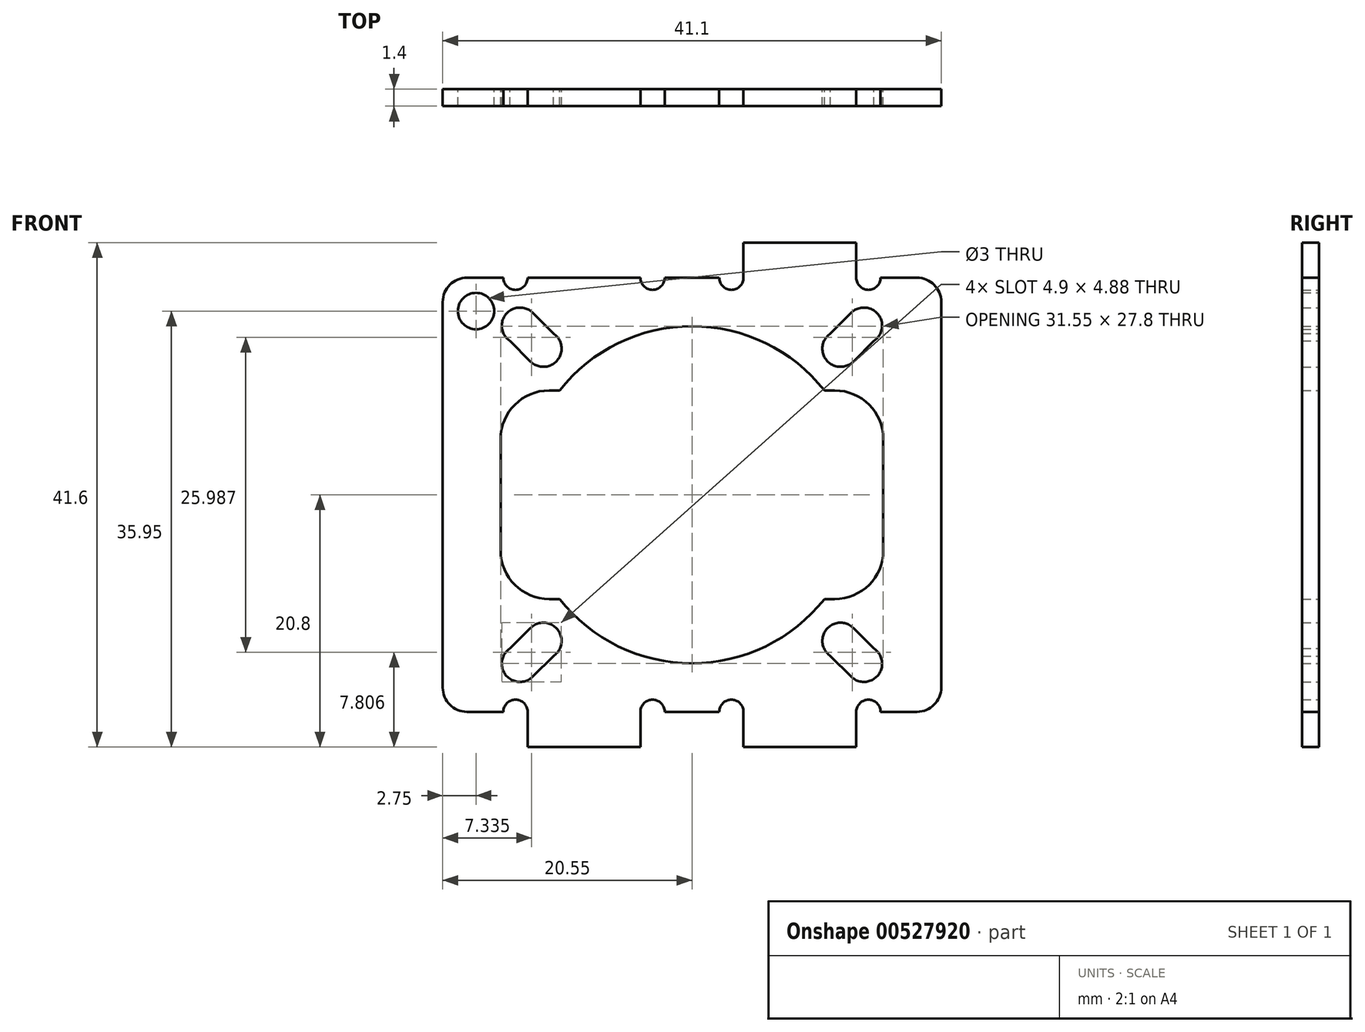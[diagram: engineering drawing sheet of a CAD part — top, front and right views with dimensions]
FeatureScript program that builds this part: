
annotation { "Feature Type Name" : "Feature", "Feature Type Description" : "" }
export const myFeature = defineFeature(function(context is Context, id is Id, definition is map)
    precondition{}
    {
        {
            var Q0;
            Q0=qCreatedBy(makeId("Front.planeOp"),FACE);
            var sketch = newSketch(context, id + "F0", { "sketchPlane" : qUnion([Q0])});
            skLineSegment(sketch, "E0.bottom", {"start": v(20.55, -17.9) * mm, "end": v(-20.55, -17.9) * mm});
            skLineSegment(sketch, "E0.top", {"start": v(20.55, 17.9) * mm, "end": v(-20.55, 17.9) * mm});
            skLineSegment(sketch, "E0.left", {"start": v(20.55, -17.9) * mm, "end": v(20.55, 17.9) * mm});
            skLineSegment(sketch, "E0.right", {"start": v(-20.55, -17.9) * mm, "end": v(-20.55, 17.9) * mm});
            skPoint(sketch, "E0.middle", {"position": v(0, 0) * mm});
            skCircle(sketch, "E1", {"center": v(0, 0) * mm, "radius": 13.9 * mm});
            skLineSegment(sketch, "E2.bottom", {"start": v(15.78, -8.6) * mm, "end": v(-15.78, -8.6) * mm});
            skLineSegment(sketch, "E2.top", {"start": v(15.78, 8.6) * mm, "end": v(-15.78, 8.6) * mm});
            skLineSegment(sketch, "E2.left", {"start": v(15.78, -8.6) * mm, "end": v(15.78, 8.6) * mm});
            skLineSegment(sketch, "E2.right", {"start": v(-15.78, -8.6) * mm, "end": v(-15.78, 8.6) * mm});
            skCircle(sketch, "E3", {"center": v(-14.18, 13.94) * mm, "radius": 1.5 * mm});
            skCircle(sketch, "E4", {"center": v(-12.25, 12.05) * mm, "radius": 1.5 * mm});
            skLineSegment(sketch, "E5", {"start": v(-15, 12.68) * mm, "end": v(-13.31, 10.99) * mm});
            skLineSegment(sketch, "E6", {"start": v(-11, 12.87) * mm, "end": v(-13.12, 15) * mm});
            skLineSegment(sketch, "E7.MirrorCS", {"start": v(-15, -12.68) * mm, "end": v(-13.31, -10.99) * mm});
            skCircle(sketch, "E8.MirrorC", {"center": v(-14.18, -13.94) * mm, "radius": 1.5 * mm});
            skCircle(sketch, "E9.MirrorC", {"center": v(-12.25, -12.05) * mm, "radius": 1.5 * mm});
            skLineSegment(sketch, "E10.MirrorCS", {"start": v(-11, -12.87) * mm, "end": v(-13.12, -15) * mm});
            skCircle(sketch, "E11.MirrorC", {"center": v(14.18, 13.94) * mm, "radius": 1.5 * mm});
            skCircle(sketch, "E12.MirrorC", {"center": v(12.25, 12.05) * mm, "radius": 1.5 * mm});
            skLineSegment(sketch, "E13.MirrorCS", {"start": v(15, 12.68) * mm, "end": v(13.31, 10.99) * mm});
            skLineSegment(sketch, "E14.MirrorCS", {"start": v(11, 12.87) * mm, "end": v(13.12, 15) * mm});
            skLineSegment(sketch, "E15.MirrorCS", {"start": v(15, -12.68) * mm, "end": v(13.31, -10.99) * mm});
            skCircle(sketch, "E16.MirrorC", {"center": v(14.18, -13.94) * mm, "radius": 1.5 * mm});
            skCircle(sketch, "E17.MirrorC", {"center": v(12.25, -12.05) * mm, "radius": 1.5 * mm});
            skLineSegment(sketch, "E18.MirrorCS", {"start": v(11, -12.87) * mm, "end": v(13.12, -15) * mm});
            skLineSegment(sketch, "E19", {"start": v(-28.19, 10.55) * mm, "end": v(24.82, 10.55) * mm, "construction": true});
            skLineSegment(sketch, "E20", {"start": v(-10.75, 26.36) * mm, "end": v(-10.75, 2.07) * mm, "construction": true});
            skLineSegment(sketch, "E21.bottom", {"start": v(-13.55, 17.9) * mm, "end": v(-4.25, 17.9) * mm});
            skLineSegment(sketch, "E21.top", {"start": v(-13.55, 20.8) * mm, "end": v(-4.25, 20.8) * mm});
            skLineSegment(sketch, "E21.left", {"start": v(-13.55, 17.9) * mm, "end": v(-13.55, 20.8) * mm});
            skLineSegment(sketch, "E21.right", {"start": v(-4.25, 17.9) * mm, "end": v(-4.25, 20.8) * mm});
            skLineSegment(sketch, "E22.MirrorCS", {"start": v(4.25, 17.9) * mm, "end": v(4.25, 20.8) * mm});
            skLineSegment(sketch, "E23.MirrorCS", {"start": v(13.55, 20.8) * mm, "end": v(4.25, 20.8) * mm});
            skLineSegment(sketch, "E24.MirrorCS", {"start": v(13.55, 17.9) * mm, "end": v(13.55, 20.8) * mm});
            skLineSegment(sketch, "E25.MirrorCS", {"start": v(-13.55, -17.9) * mm, "end": v(-13.55, -20.8) * mm});
            skLineSegment(sketch, "E26.MirrorCS", {"start": v(-13.55, -20.8) * mm, "end": v(-4.25, -20.8) * mm});
            skLineSegment(sketch, "E27.MirrorCS", {"start": v(-4.25, -17.9) * mm, "end": v(-4.25, -20.8) * mm});
            skLineSegment(sketch, "E28.MirrorCS", {"start": v(4.25, -17.9) * mm, "end": v(4.25, -20.8) * mm});
            skLineSegment(sketch, "E29.MirrorCS", {"start": v(13.55, -20.8) * mm, "end": v(4.25, -20.8) * mm});
            skLineSegment(sketch, "E30.MirrorCS", {"start": v(13.55, -17.9) * mm, "end": v(13.55, -20.8) * mm});
            skCircle(sketch, "E31", {"center": v(3.25, 17.9) * mm, "radius": 1 * mm});
            skCircle(sketch, "E32", {"center": v(-3.25, 17.9) * mm, "radius": 1 * mm});
            skCircle(sketch, "E33", {"center": v(-14.55, 17.9) * mm, "radius": 1 * mm});
            skCircle(sketch, "E34.MirrorC", {"center": v(-14.55, -17.9) * mm, "radius": 1 * mm});
            skCircle(sketch, "E35.MirrorC", {"center": v(-3.25, -17.9) * mm, "radius": 1 * mm});
            skCircle(sketch, "E36.MirrorC", {"center": v(3.25, -17.9) * mm, "radius": 1 * mm});
            skCircle(sketch, "E37", {"center": v(14.55, 17.9) * mm, "radius": 1 * mm});
            skCircle(sketch, "E38.MirrorC", {"center": v(14.55, -17.9) * mm, "radius": 1 * mm});
            skCircle(sketch, "E39", {"center": v(-17.8, 15.15) * mm, "radius": 1.5 * mm});
            skSolve(sketch);
        }
        {
            var Q0;
            Q0=makeQuery(id+"F0.imprint","IMPRINT",FACE,{"disambiguationData":[TD([[makeQuery(id+"F0.imprint","IMPRINT",EDGE,{"derivedFrom":sQuery(id+"F0.wireOp",EDGE,"E0.bottom")}),-1.0]])]});
            var Q1;
            Q1=makeQuery(id+"F0.imprint","IMPRINT",FACE,{"disambiguationData":[TD([[makeQuery(id+"F0.imprint","IMPRINT",EDGE,{"derivedFrom":sQuery(id+"F0.wireOp",EDGE,"E21.bottom")}),1.0]])]});
            var Q2;
            {var subQ0=sQuery(id+"F0.wireOp",EDGE,"E25.MirrorCS");Q2=makeQuery(id+"F0.imprint","IMPRINT",FACE,{"disambiguationData":[TD([[makeQuery(id+"F0.imprint","IMPRINT",EDGE,{"derivedFrom":subQ0}),1.0]])]});}
            var Q3;
            {var subQ0=sQuery(id+"F0.wireOp",EDGE,"E28.MirrorCS");Q3=makeQuery(id+"F0.imprint","IMPRINT",FACE,{"disambiguationData":[TD([[makeQuery(id+"F0.imprint","IMPRINT",EDGE,{"derivedFrom":subQ0}),1.0]])]});}
            var Q4;
            {var subQ0=sQuery(id+"F0.wireOp",EDGE,"E22.MirrorCS");Q4=makeQuery(id+"F0.imprint","IMPRINT",FACE,{"disambiguationData":[TD([[makeQuery(id+"F0.imprint","IMPRINT",EDGE,{"derivedFrom":subQ0}),-1.0]])]});}
            extrude(context, id + "F1", {"entities" : qUnion([Q0, Q1, Q2, Q3, Q4]), "depth" : 1.4 * mm, "offsetDistance" : 25 * mm});
        }
        {
            var Q0;
            Q0=makeQuery(id+"F1.opExtrude","SWEPT_EDGE",EDGE,{"disambiguationData":[OSD([sQuery(id+"F0.wireOp",EDGE,"E2.top"),sQuery(id+"F0.wireOp",EDGE,"E2.right")])]});
            var Q1;
            Q1=makeQuery(id+"F1.opExtrude","SWEPT_EDGE",EDGE,{"disambiguationData":[OSD([sQuery(id+"F0.wireOp",EDGE,"E2.bottom"),sQuery(id+"F0.wireOp",EDGE,"E2.right")])]});
            var Q2;
            Q2=makeQuery(id+"F1.opExtrude","SWEPT_EDGE",EDGE,{"disambiguationData":[OSD([sQuery(id+"F0.wireOp",EDGE,"E2.top"),sQuery(id+"F0.wireOp",EDGE,"E2.left")])]});
            var Q3;
            Q3=makeQuery(id+"F1.opExtrude","SWEPT_EDGE",EDGE,{"disambiguationData":[OSD([sQuery(id+"F0.wireOp",EDGE,"E2.bottom"),sQuery(id+"F0.wireOp",EDGE,"E2.left")])]});
            fillet(context, id + "F2", {"entities" : qUnion([Q0, Q1, Q2, Q3]), "radius" : 4 * mm, "tangentPropagation" : true, "allowEdgeOverflow" : false});
        }
        {
            var Q0;
            {var subQ0=sQuery(id+"F0.wireOp",EDGE,"E33");var subQ1=sQuery(id+"F0.wireOp",EDGE,"E0.top");var subQ3=makeQuery(id+"F0.imprint","INTERSECT",VERTEX,{"derivedFrom":[subQ1,subQ0]});Q0=makeQuery(id+"F0.imprint","IMPRINT",FACE,{"disambiguationData":[TD([[makeQuery(id+"F0.imprint","IMPRINT",EDGE,{"disambiguationData":[TD([[subQ3,1.0]])],"derivedFrom":subQ1}),1.0]])]});}
            var Q1;
            {var subQ0=sQuery(id+"F0.wireOp",EDGE,"E33");var subQ1=sQuery(id+"F0.wireOp",EDGE,"E0.top");var subQ3=makeQuery(id+"F0.imprint","INTERSECT",VERTEX,{"derivedFrom":[subQ1,subQ0]});Q1=makeQuery(id+"F0.imprint","IMPRINT",FACE,{"disambiguationData":[TD([[makeQuery(id+"F0.imprint","IMPRINT",EDGE,{"disambiguationData":[TD([[subQ3,1.0]])],"derivedFrom":subQ1}),-1.0]])]});}
            var Q2;
            {var subQ0=sQuery(id+"F0.wireOp",EDGE,"E32");var subQ1=sQuery(id+"F0.wireOp",EDGE,"E0.top");var subQ3=makeQuery(id+"F0.imprint","INTERSECT",VERTEX,{"derivedFrom":[subQ1,subQ0]});Q2=makeQuery(id+"F0.imprint","IMPRINT",FACE,{"disambiguationData":[TD([[makeQuery(id+"F0.imprint","IMPRINT",EDGE,{"disambiguationData":[TD([[subQ3,-1.0]])],"derivedFrom":subQ1}),1.0]])]});}
            var Q3;
            {var subQ0=sQuery(id+"F0.wireOp",EDGE,"E32");var subQ1=sQuery(id+"F0.wireOp",EDGE,"E0.top");var subQ3=makeQuery(id+"F0.imprint","INTERSECT",VERTEX,{"derivedFrom":[subQ1,subQ0]});Q3=makeQuery(id+"F0.imprint","IMPRINT",FACE,{"disambiguationData":[TD([[makeQuery(id+"F0.imprint","IMPRINT",EDGE,{"disambiguationData":[TD([[subQ3,-1.0]])],"derivedFrom":subQ1}),-1.0]])]});}
            var Q4;
            {var subQ0=sQuery(id+"F0.wireOp",EDGE,"E31");var subQ1=sQuery(id+"F0.wireOp",EDGE,"E0.top");var subQ3=makeQuery(id+"F0.imprint","INTERSECT",VERTEX,{"derivedFrom":[subQ1,subQ0]});Q4=makeQuery(id+"F0.imprint","IMPRINT",FACE,{"disambiguationData":[TD([[makeQuery(id+"F0.imprint","IMPRINT",EDGE,{"disambiguationData":[TD([[subQ3,1.0]])],"derivedFrom":subQ1}),1.0]])]});}
            var Q5;
            {var subQ0=sQuery(id+"F0.wireOp",EDGE,"E31");var subQ1=sQuery(id+"F0.wireOp",EDGE,"E0.top");var subQ3=makeQuery(id+"F0.imprint","INTERSECT",VERTEX,{"derivedFrom":[subQ1,subQ0]});Q5=makeQuery(id+"F0.imprint","IMPRINT",FACE,{"disambiguationData":[TD([[makeQuery(id+"F0.imprint","IMPRINT",EDGE,{"disambiguationData":[TD([[subQ3,1.0]])],"derivedFrom":subQ1}),-1.0]])]});}
            var Q6;
            {var subQ0=sQuery(id+"F0.wireOp",EDGE,"hedvDMrz-FKNq-aqVW-e1ld-ApxuIKkpfcKG");var subQ1=sQuery(id+"F0.wireOp",EDGE,"E0.top");var subQ2=makeQuery(id+"F0.imprint","INTERSECT",VERTEX,{"disambiguationData":[OD(0.0)],"derivedFrom":[subQ1,subQ0]});Q6=makeQuery(id+"F0.imprint","IMPRINT",FACE,{"disambiguationData":[TD([[makeQuery(id+"F0.imprint","IMPRINT",EDGE,{"disambiguationData":[TD([[subQ2,-1.0]])],"derivedFrom":subQ1}),1.0]])]});}
            var Q7;
            {var subQ0=sQuery(id+"F0.wireOp",EDGE,"hedvDMrz-FKNq-aqVW-e1ld-ApxuIKkpfcKG");var subQ1=sQuery(id+"F0.wireOp",EDGE,"E0.top");var subQ2=makeQuery(id+"F0.imprint","INTERSECT",VERTEX,{"disambiguationData":[OD(0.0)],"derivedFrom":[subQ1,subQ0]});Q7=makeQuery(id+"F0.imprint","IMPRINT",FACE,{"disambiguationData":[TD([[makeQuery(id+"F0.imprint","IMPRINT",EDGE,{"disambiguationData":[TD([[subQ2,-1.0]])],"derivedFrom":subQ1}),-1.0]])]});}
            extrude(context, id + "F3", {"entities" : qUnion([Q0, Q1, Q2, Q3, Q4, Q5, Q6, Q7]), "operationType" : NewBodyOperationType.REMOVE, "depth" : 2 * mm, "offsetDistance" : 25 * mm});
        }
        {
            var Q0;
            Q0=makeQuery(id+"F1.opExtrude","SWEPT_EDGE",EDGE,{"disambiguationData":[OSD([sQuery(id+"F0.wireOp",EDGE,"E0.top"),sQuery(id+"F0.wireOp",EDGE,"E0.right")])]});
            var Q1;
            Q1=makeQuery(id+"F1.opExtrude","SWEPT_EDGE",EDGE,{"disambiguationData":[OSD([sQuery(id+"F0.wireOp",EDGE,"E0.top"),sQuery(id+"F0.wireOp",EDGE,"E0.left")])]});
            var Q2;
            Q2=makeQuery(id+"F1.opExtrude","SWEPT_EDGE",EDGE,{"disambiguationData":[OSD([sQuery(id+"F0.wireOp",EDGE,"E0.bottom"),sQuery(id+"F0.wireOp",EDGE,"E0.left")])]});
            var Q3;
            Q3=makeQuery(id+"F1.opExtrude","SWEPT_EDGE",EDGE,{"disambiguationData":[OSD([sQuery(id+"F0.wireOp",EDGE,"E0.bottom"),sQuery(id+"F0.wireOp",EDGE,"E0.right")])]});
            fillet(context, id + "F4", {"entities" : qUnion([Q0, Q1, Q2, Q3]), "radius" : 2 * mm, "tangentPropagation" : true, "allowEdgeOverflow" : false});
        }
    });
